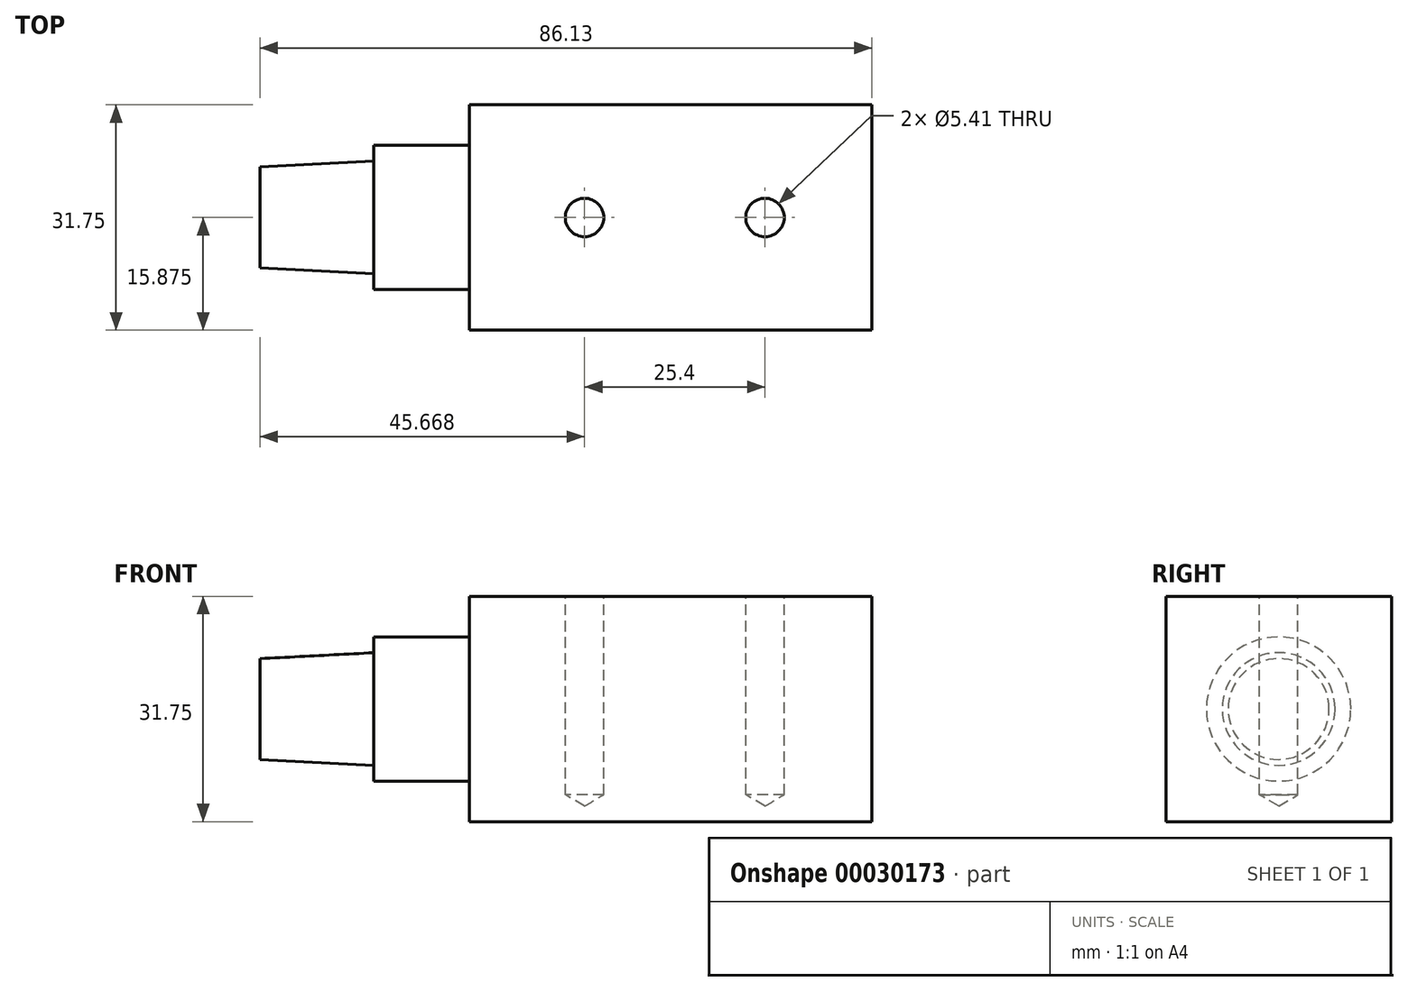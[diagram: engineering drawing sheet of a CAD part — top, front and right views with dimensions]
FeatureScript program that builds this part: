
annotation { "Feature Type Name" : "Feature", "Feature Type Description" : "" }
export const myFeature = defineFeature(function(context is Context, id is Id, definition is map)
    precondition{}
    {
        {
            var Q0;
            Q0=qCreatedBy(makeId("Top.planeOp"),FACE);
            var sketch = newSketch(context, id + "F0", { "sketchPlane" : qUnion([Q0])});
            skLineSegment(sketch, "E0.bottom", {"start": v(0, 0) * mm, "end": v(-56.64, 0) * mm});
            skLineSegment(sketch, "E0.top", {"start": v(0, -31.75) * mm, "end": v(-56.64, -31.75) * mm});
            skLineSegment(sketch, "E0.left", {"start": v(0, 0) * mm, "end": v(0, -31.75) * mm});
            skLineSegment(sketch, "E0.right", {"start": v(-56.64, 0) * mm, "end": v(-56.64, -31.75) * mm});
            skSolve(sketch);
        }
        {
            var Q0;
            Q0=makeQuery(id+"F0.imprint","IMPRINT",FACE,{"disambiguationData":[TD([[makeQuery(id+"F0.imprint","IMPRINT",EDGE,{"derivedFrom":sQuery(id+"F0.wireOp",EDGE,"E0.bottom")}),1.0]])]});
            extrude(context, id + "F1", {"entities" : qUnion([Q0]), "oppositeDirection" : true, "depth" : 31.75 * mm});
        }
        {
            var Q0;
            Q0=makeQuery(id+"F1.opExtrude","SWEPT_FACE",FACE,{"disambiguationData":[OSD([sQuery(id+"F0.wireOp",EDGE,"E0.right")])]});
            var sketch = newSketch(context, id + "F2", { "sketchPlane" : qUnion([Q0])});
            skCircle(sketch, "E1", {"center": v(15.88, -15.87) * mm, "radius": 10.16 * mm});
            skSolve(sketch);
        }
        {
            var Q0;
            Q0 = qSketchRegion(id + "F2", true);
            extrude(context, id + "F3", {"entities" : qUnion([Q0]), "operationType" : NewBodyOperationType.ADD, "depth" : 13.5 * mm});
        }
        {
            var Q0;
            Q0=makeQuery(id+"F3.opExtrude","CAP_FACE",FACE,{"disambiguationData":[OSD([sQuery(id+"F2.wireOp",EDGE,"E1")])],"isStart":false});
            var sketch = newSketch(context, id + "F4", { "sketchPlane" : qUnion([Q0])});
            skCircle(sketch, "E2", {"center": v(15.88, -15.87) * mm, "radius": 7.94 * mm});
            skSolve(sketch);
        }
        {
            var Q0;
            Q0=makeQuery(id+"F4.imprint","IMPRINT",FACE,{"disambiguationData":[TD([[makeQuery(id+"F4.imprint","IMPRINT",EDGE,{"derivedFrom":sQuery(id+"F4.wireOp",EDGE,"E2")}),1.0]])]});
            extrude(context, id + "F5", {"entities" : qUnion([Q0]), "operationType" : NewBodyOperationType.ADD, "depth" : 16 * mm, "hasDraft" : true, "draftAngle" : 3 * degree, "draftPullDirection" : true});
        }
        {
            var Q0;
            Q0=makeQuery(id+"F1.opExtrude","CAP_FACE",FACE,{"disambiguationData":[OSD([sQuery(id+"F0.wireOp",EDGE,"E0.bottom"),sQuery(id+"F0.wireOp",EDGE,"E0.top"),sQuery(id+"F0.wireOp",EDGE,"E0.left"),sQuery(id+"F0.wireOp",EDGE,"E0.right")])],"isStart":true});
            var sketch = newSketch(context, id + "F6", { "sketchPlane" : qUnion([Q0])});
            skPoint(sketch, "E3", {"position": v(-15.06, -15.88) * mm});
            skPoint(sketch, "E4", {"position": v(-40.46, -15.88) * mm});
            skSolve(sketch);
        }
        {
            var Q0;
            Q0=sQuery(id+"F6.wireOp",VERTEX,"E3");
            var Q1;
            Q1=sQuery(id+"F6.wireOp",VERTEX,"E4");
            var Q2;
            Q2=makeQuery(id+"F1.opExtrude","SWEPT_BODY",BODY,{"disambiguationData":[OSD([sQuery(id+"F0.wireOp",EDGE,"E0.bottom"),sQuery(id+"F0.wireOp",EDGE,"E0.top"),sQuery(id+"F0.wireOp",EDGE,"E0.left"),sQuery(id+"F0.wireOp",EDGE,"E0.right")])]});
            hole(context, id + "F7", {"style" : HoleStyle.SIMPLE, "holeDiameter" : 5.4 * mm, "endStyle" : HoleEndStyle.BLIND, "holeDepth" : 27.94 * mm, "locations" : qUnion([Q0, Q1]), "scope" : qUnion([Q2])});
        }
    });
